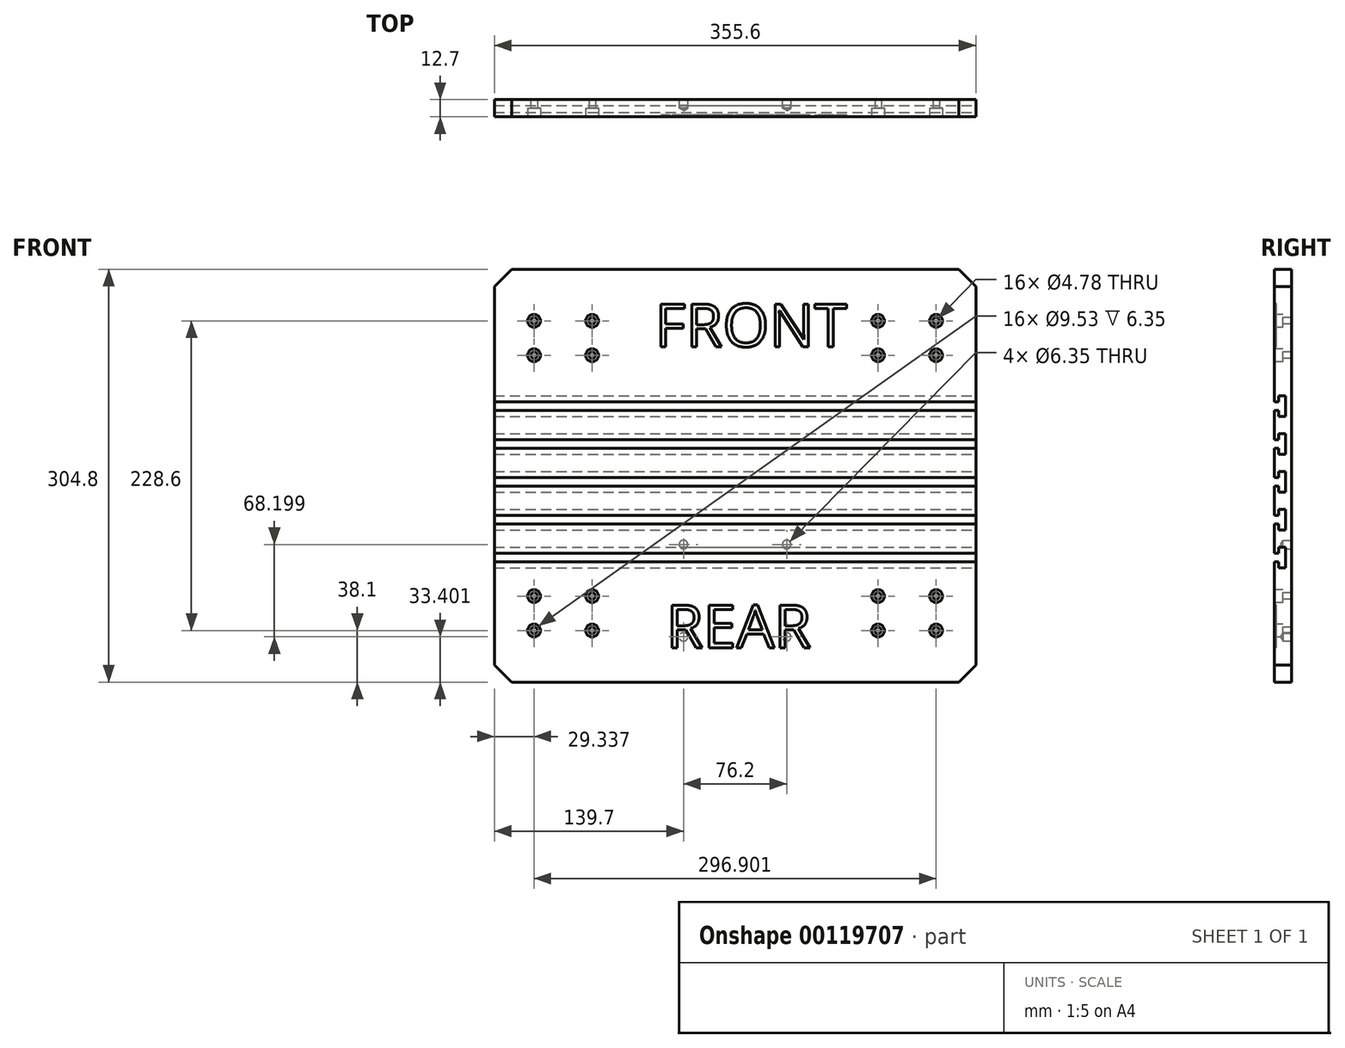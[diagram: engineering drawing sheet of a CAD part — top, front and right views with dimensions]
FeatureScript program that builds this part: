
annotation { "Feature Type Name" : "Feature", "Feature Type Description" : "" }
export const myFeature = defineFeature(function(context is Context, id is Id, definition is map)
    precondition{}
    {
        {
            var Q0;
            Q0=qCreatedBy(makeId("Front.planeOp"),FACE);
            var sketch = newSketch(context, id + "F0", { "sketchPlane" : qUnion([Q0])});
            skLineSegment(sketch, "E0.bottom", {"start": v(0, 0) * mm, "end": v(355.6, 0) * mm});
            skLineSegment(sketch, "E0.top", {"start": v(0, 304.8) * mm, "end": v(355.6, 304.8) * mm});
            skLineSegment(sketch, "E0.left", {"start": v(0, 0) * mm, "end": v(0, 304.8) * mm});
            skLineSegment(sketch, "E0.right", {"start": v(355.6, 0) * mm, "end": v(355.6, 304.8) * mm});
            skSolve(sketch);
        }
        {
            var Q0;
            Q0 = qSketchRegion(id + "F0", true);
            extrude(context, id + "F1", {"entities" : qUnion([Q0]), "depth" : 12.7 * mm});
        }
        {
            var Q0;
            Q0=makeQuery(id+"F1.opExtrude","CAP_FACE",FACE,{"disambiguationData":[OSD([sQuery(id+"F0.wireOp",EDGE,"E0.bottom"),sQuery(id+"F0.wireOp",EDGE,"E0.top"),sQuery(id+"F0.wireOp",EDGE,"E0.left"),sQuery(id+"F0.wireOp",EDGE,"E0.right")])],"isStart":false});
            var sketch = newSketch(context, id + "F2", { "sketchPlane" : qUnion([Q0])});
            skSolve(sketch);
        }
        {
            var Q0;
            Q0=makeQuery(id+"F2.imprint","IMPRINT",FACE,{"disambiguationData":[TD([[makeQuery(id+"F2.imprint","IMPRINT",EDGE,{"derivedFrom":makeQuery(id+"F1.opExtrude","CAP_EDGE",EDGE,{"disambiguationData":[OSD([sQuery(id+"F0.wireOp",EDGE,"E0.bottom")])],"isStart":false})}),1.0]])]});
            var sketch = newSketch(context, id + "F3", { "sketchPlane" : qUnion([Q0])});
            skLineSegment(sketch, "E1.bottom", {"start": v(72.21, 266.7) * mm, "end": v(283.36, 266.7) * mm, "construction": true});
            skLineSegment(sketch, "E1.top", {"start": v(72.21, 38.1) * mm, "end": v(283.36, 38.1) * mm, "construction": true});
            skLineSegment(sketch, "E1.left", {"start": v(72.21, 266.7) * mm, "end": v(72.21, 38.1) * mm, "construction": true});
            skLineSegment(sketch, "E1.right", {"start": v(283.36, 266.7) * mm, "end": v(283.36, 38.1) * mm, "construction": true});
            skPoint(sketch, "E2", {"position": v(72.21, 266.7) * mm});
            skPoint(sketch, "E3", {"position": v(283.36, 266.7) * mm});
            skPoint(sketch, "E4", {"position": v(283.36, 38.1) * mm});
            skPoint(sketch, "E5", {"position": v(72.21, 38.1) * mm});
            skPoint(sketch, "E6", {"position": v(29.34, 266.7) * mm});
            skPoint(sketch, "E7", {"position": v(326.24, 266.7) * mm});
            skPoint(sketch, "E8", {"position": v(326.24, 38.1) * mm});
            skPoint(sketch, "E9", {"position": v(29.34, 38.1) * mm});
            skPoint(sketch, "E10", {"position": v(29.34, 241.3) * mm});
            skPoint(sketch, "E11", {"position": v(72.21, 241.3) * mm});
            skPoint(sketch, "E12", {"position": v(326.24, 241.3) * mm});
            skPoint(sketch, "E13", {"position": v(283.36, 241.3) * mm});
            skPoint(sketch, "E14", {"position": v(72.21, 63.5) * mm});
            skPoint(sketch, "E15", {"position": v(29.34, 63.5) * mm});
            skPoint(sketch, "E16", {"position": v(283.36, 63.5) * mm});
            skPoint(sketch, "E17", {"position": v(326.24, 63.5) * mm});
            skSolve(sketch);
        }
        {
            var Q0;
            Q0=sQuery(id+"F3.wireOp",VERTEX,"E6");
            var Q1;
            Q1=sQuery(id+"F3.wireOp",VERTEX,"E2");
            var Q2;
            Q2=sQuery(id+"F3.wireOp",VERTEX,"E11");
            var Q3;
            Q3=sQuery(id+"F3.wireOp",VERTEX,"E10");
            var Q4;
            Q4=sQuery(id+"F3.wireOp",VERTEX,"E15");
            var Q5;
            Q5=sQuery(id+"F3.wireOp",VERTEX,"E14");
            var Q6;
            Q6=sQuery(id+"F3.wireOp",VERTEX,"E5");
            var Q7;
            Q7=sQuery(id+"F3.wireOp",VERTEX,"E9");
            var Q8;
            Q8=sQuery(id+"F3.wireOp",VERTEX,"E4");
            var Q9;
            Q9=sQuery(id+"F3.wireOp",VERTEX,"E16");
            var Q10;
            Q10=sQuery(id+"F3.wireOp",VERTEX,"E17");
            var Q11;
            Q11=sQuery(id+"F3.wireOp",VERTEX,"E8");
            var Q12;
            Q12=sQuery(id+"F3.wireOp",VERTEX,"E13");
            var Q13;
            Q13=sQuery(id+"F3.wireOp",VERTEX,"E12");
            var Q14;
            Q14=sQuery(id+"F3.wireOp",VERTEX,"E7");
            var Q15;
            Q15=sQuery(id+"F3.wireOp",VERTEX,"E3");
            var Q16;
            Q16=makeQuery(id+"F1.opExtrude","SWEPT_BODY",BODY,{"disambiguationData":[OSD([sQuery(id+"F0.wireOp",EDGE,"E0.bottom"),sQuery(id+"F0.wireOp",EDGE,"E0.top"),sQuery(id+"F0.wireOp",EDGE,"E0.left"),sQuery(id+"F0.wireOp",EDGE,"E0.right")])]});
            hole(context, id + "F4", {"style" : HoleStyle.C_BORE, "endStyle" : HoleEndStyle.THROUGH, "holeDiameter" : 4.78 * mm, "cBoreDiameter" : 9.52 * mm, "cBoreDepth" : 6.35 * mm, "locations" : qUnion([Q0, Q1, Q2, Q3, Q4, Q5, Q6, Q7, Q8, Q9, Q10, Q11, Q12, Q13, Q14, Q15]), "scope" : qUnion([Q16]), "isTappedThrough" : true});
        }
        {
            var Q0;
            Q0=makeQuery(id+"F1.opExtrude","SWEPT_FACE",FACE,{"disambiguationData":[OSD([sQuery(id+"F0.wireOp",EDGE,"E0.right")])]});
            var sketch = newSketch(context, id + "F5", { "sketchPlane" : qUnion([Q0])});
            skLineSegment(sketch, "E18", {"start": v(-12.7, 88.9) * mm, "end": v(-9.53, 88.9) * mm});
            skLineSegment(sketch, "E19", {"start": v(-9.53, 88.9) * mm, "end": v(-9.53, 84.45) * mm});
            skLineSegment(sketch, "E20", {"start": v(-9.52, 84.45) * mm, "end": v(-4.44, 84.45) * mm});
            skLineSegment(sketch, "E21", {"start": v(-4.44, 84.45) * mm, "end": v(-4.45, 99.7) * mm});
            skLineSegment(sketch, "E22", {"start": v(-4.45, 99.7) * mm, "end": v(-9.53, 99.7) * mm});
            skLineSegment(sketch, "E23", {"start": v(-9.53, 99.7) * mm, "end": v(-9.53, 95.25) * mm});
            skLineSegment(sketch, "E24", {"start": v(-9.53, 95.25) * mm, "end": v(-12.7, 95.25) * mm});
            skLineSegment(sketch, "E25", {"start": v(-12.7, 116.84) * mm, "end": v(-9.52, 116.84) * mm});
            skLineSegment(sketch, "E26", {"start": v(-9.52, 116.84) * mm, "end": v(-9.52, 112.4) * mm});
            skLineSegment(sketch, "E27", {"start": v(-9.52, 112.4) * mm, "end": v(-4.44, 112.4) * mm});
            skLineSegment(sketch, "E28", {"start": v(-4.44, 112.4) * mm, "end": v(-4.45, 127.64) * mm});
            skLineSegment(sketch, "E29", {"start": v(-4.45, 127.64) * mm, "end": v(-9.53, 127.64) * mm});
            skLineSegment(sketch, "E30", {"start": v(-9.53, 127.64) * mm, "end": v(-9.53, 123.19) * mm});
            skLineSegment(sketch, "E31", {"start": v(-9.52, 123.19) * mm, "end": v(-12.7, 123.19) * mm});
            skLineSegment(sketch, "E32", {"start": v(-12.7, 151.13) * mm, "end": v(-9.53, 151.13) * mm});
            skLineSegment(sketch, "E33", {"start": v(-9.53, 151.13) * mm, "end": v(-9.53, 155.57) * mm});
            skLineSegment(sketch, "E34", {"start": v(-9.53, 155.57) * mm, "end": v(-4.45, 155.57) * mm});
            skLineSegment(sketch, "E35", {"start": v(-4.45, 155.57) * mm, "end": v(-4.45, 140.33) * mm});
            skLineSegment(sketch, "E36", {"start": v(-4.45, 140.33) * mm, "end": v(-9.53, 140.33) * mm});
            skLineSegment(sketch, "E37", {"start": v(-9.53, 140.33) * mm, "end": v(-9.53, 144.78) * mm});
            skLineSegment(sketch, "E38", {"start": v(-9.53, 144.78) * mm, "end": v(-12.7, 144.78) * mm});
            skLineSegment(sketch, "E39", {"start": v(-12.7, 144.78) * mm, "end": v(-12.7, 151.13) * mm});
            skLineSegment(sketch, "E40", {"start": v(-12.7, 179.07) * mm, "end": v(-9.53, 179.07) * mm});
            skLineSegment(sketch, "E41", {"start": v(-9.53, 179.07) * mm, "end": v(-9.53, 183.51) * mm});
            skLineSegment(sketch, "E42", {"start": v(-9.53, 183.51) * mm, "end": v(-4.45, 183.51) * mm});
            skLineSegment(sketch, "E43", {"start": v(-4.45, 183.51) * mm, "end": v(-4.45, 168.27) * mm});
            skLineSegment(sketch, "E44", {"start": v(-4.45, 168.27) * mm, "end": v(-9.53, 168.27) * mm});
            skLineSegment(sketch, "E45", {"start": v(-9.53, 168.27) * mm, "end": v(-9.53, 172.72) * mm});
            skLineSegment(sketch, "E46", {"start": v(-9.53, 172.72) * mm, "end": v(-12.7, 172.72) * mm});
            skLineSegment(sketch, "E47", {"start": v(-12.7, 172.72) * mm, "end": v(-12.7, 179.07) * mm});
            skLineSegment(sketch, "E48", {"start": v(-12.7, 207) * mm, "end": v(-9.53, 207) * mm});
            skLineSegment(sketch, "E49", {"start": v(-9.53, 207) * mm, "end": v(-9.53, 211.45) * mm});
            skLineSegment(sketch, "E50", {"start": v(-9.53, 211.45) * mm, "end": v(-4.45, 211.45) * mm});
            skLineSegment(sketch, "E51", {"start": v(-4.45, 211.45) * mm, "end": v(-4.44, 196.21) * mm});
            skLineSegment(sketch, "E52", {"start": v(-4.44, 196.21) * mm, "end": v(-9.53, 196.21) * mm});
            skLineSegment(sketch, "E53", {"start": v(-9.52, 196.21) * mm, "end": v(-9.52, 200.66) * mm});
            skLineSegment(sketch, "E54", {"start": v(-9.53, 200.66) * mm, "end": v(-12.7, 200.66) * mm});
            skLineSegment(sketch, "E55", {"start": v(-12.7, 200.66) * mm, "end": v(-12.7, 207) * mm});
            skSolve(sketch);
        }
        {
            var Q0;
            Q0 = qSketchRegion(id + "F5", true);
            var Q1;
            {var subQ0=sQuery(id+"F5.wireOp",EDGE,"E25");Q1=makeQuery(id+"F5.imprint","IMPRINT",FACE,{"disambiguationData":[TD([[makeQuery(id+"F5.imprint","IMPRINT",EDGE,{"derivedFrom":subQ0}),1.0]])]});}
            var Q2;
            {var subQ0=sQuery(id+"F5.wireOp",EDGE,"E18");Q2=makeQuery(id+"F5.imprint","IMPRINT",FACE,{"disambiguationData":[TD([[makeQuery(id+"F5.imprint","IMPRINT",EDGE,{"derivedFrom":subQ0}),1.0]])]});}
            extrude(context, id + "F6", {"entities" : qUnion([Q0, Q1, Q2]), "operationType" : NewBodyOperationType.REMOVE, "endBound" : BoundingType.THROUGH_ALL, "oppositeDirection" : true, "depth" : 25.4 * mm});
        }
        {
            var Q0;
            Q0=makeQuery(id+"F2.imprint","IMPRINT",FACE,{"disambiguationData":[TD([[makeQuery(id+"F2.imprint","IMPRINT",EDGE,{"derivedFrom":makeQuery(id+"F1.opExtrude","CAP_EDGE",EDGE,{"disambiguationData":[OSD([sQuery(id+"F0.wireOp",EDGE,"E0.bottom")])],"isStart":false})}),1.0]])]});
            var sketch = newSketch(context, id + "F7", { "sketchPlane" : qUnion([Q0])});
            skText(sketch, "E56", { "text": "FRONT", "fontName": "OpenSans-Regular.ttf"});
            const initialGuessF7  = {"E56": [0.11862, 0.24765, 1, 0, 0.03175]};
            skSetInitialGuess(sketch, initialGuessF7);
            skSolve(sketch);
        }
        {
            var Q0;
            Q0 = qSketchRegion(id + "F7", true);
            extrude(context, id + "F8", {"entities" : qUnion([Q0]), "operationType" : NewBodyOperationType.REMOVE, "oppositeDirection" : true, "depth" : 1.27 * mm});
        }
        {
            var Q0;
            Q0=makeQuery(id+"F2.imprint","IMPRINT",FACE,{"disambiguationData":[TD([[makeQuery(id+"F2.imprint","IMPRINT",EDGE,{"derivedFrom":makeQuery(id+"F1.opExtrude","CAP_EDGE",EDGE,{"disambiguationData":[OSD([sQuery(id+"F0.wireOp",EDGE,"E0.bottom")])],"isStart":false})}),1.0]])]});
            var sketch = newSketch(context, id + "F9", { "sketchPlane" : qUnion([Q0])});
            skText(sketch, "E57", { "text": "REAR\n", "fontName": "OpenSans-Regular.ttf"});
            const initialGuessF9  = {"E57": [0.127, 0.0254, 1, 0, 0.03175]};
            skSetInitialGuess(sketch, initialGuessF9);
            skSolve(sketch);
        }
        {
            var Q0;
            Q0 = qSketchRegion(id + "F9", true);
            extrude(context, id + "F10", {"entities" : qUnion([Q0]), "operationType" : NewBodyOperationType.REMOVE, "oppositeDirection" : true, "depth" : 1.27 * mm});
        }
        {
            var Q0;
            Q0=makeQuery(id+"F1.opExtrude","CAP_FACE",FACE,{"disambiguationData":[OSD([sQuery(id+"F0.wireOp",EDGE,"E0.bottom"),sQuery(id+"F0.wireOp",EDGE,"E0.top"),sQuery(id+"F0.wireOp",EDGE,"E0.left"),sQuery(id+"F0.wireOp",EDGE,"E0.right")])],"isStart":true});
            var sketch = newSketch(context, id + "F11", { "sketchPlane" : qUnion([Q0])});
            skPoint(sketch, "E58", {"position": v(-215.9, 101.6) * mm});
            skPoint(sketch, "E59", {"position": v(-139.7, 101.6) * mm});
            skPoint(sketch, "E60", {"position": v(-139.7, 33.4) * mm});
            skPoint(sketch, "E61", {"position": v(-215.9, 33.4) * mm});
            skSolve(sketch);
        }
        {
            var Q0;
            Q0=sQuery(id+"F11.wireOp",VERTEX,"E58");
            var Q1;
            Q1=sQuery(id+"F11.wireOp",VERTEX,"E61");
            var Q2;
            Q2=sQuery(id+"F11.wireOp",VERTEX,"E60");
            var Q3;
            Q3=sQuery(id+"F11.wireOp",VERTEX,"E59");
            var Q4;
            Q4=makeQuery(id+"F1.opExtrude","SWEPT_BODY",BODY,{"disambiguationData":[OSD([sQuery(id+"F0.wireOp",EDGE,"E0.bottom"),sQuery(id+"F0.wireOp",EDGE,"E0.top"),sQuery(id+"F0.wireOp",EDGE,"E0.left"),sQuery(id+"F0.wireOp",EDGE,"E0.right")])]});
            hole(context, id + "F12", {"style" : HoleStyle.SIMPLE, "endStyle" : HoleEndStyle.BLIND, "holeDiameter" : 6.35 * mm, "holeDepth" : 6.35 * mm, "locations" : qUnion([Q0, Q1, Q2, Q3]), "scope" : qUnion([Q4])});
        }
        {
            var Q0;
            Q0=makeQuery(id+"F1.opExtrude","SWEPT_EDGE",EDGE,{"disambiguationData":[OSD([sQuery(id+"F0.wireOp",EDGE,"E0.top"),sQuery(id+"F0.wireOp",EDGE,"E0.left")])]});
            var Q1;
            Q1=makeQuery(id+"F1.opExtrude","SWEPT_EDGE",EDGE,{"disambiguationData":[OSD([sQuery(id+"F0.wireOp",EDGE,"E0.bottom"),sQuery(id+"F0.wireOp",EDGE,"E0.left")])]});
            var Q2;
            Q2=makeQuery(id+"F1.opExtrude","SWEPT_EDGE",EDGE,{"disambiguationData":[OSD([sQuery(id+"F0.wireOp",EDGE,"E0.bottom"),sQuery(id+"F0.wireOp",EDGE,"E0.right")])]});
            var Q3;
            Q3=makeQuery(id+"F1.opExtrude","SWEPT_EDGE",EDGE,{"disambiguationData":[OSD([sQuery(id+"F0.wireOp",EDGE,"E0.top"),sQuery(id+"F0.wireOp",EDGE,"E0.right")])]});
            chamfer(context, id + "F13", {"entities" : qUnion([Q0, Q1, Q2, Q3]), "width" : 12.7 * mm, "tangentPropagation" : true});
        }
    });
